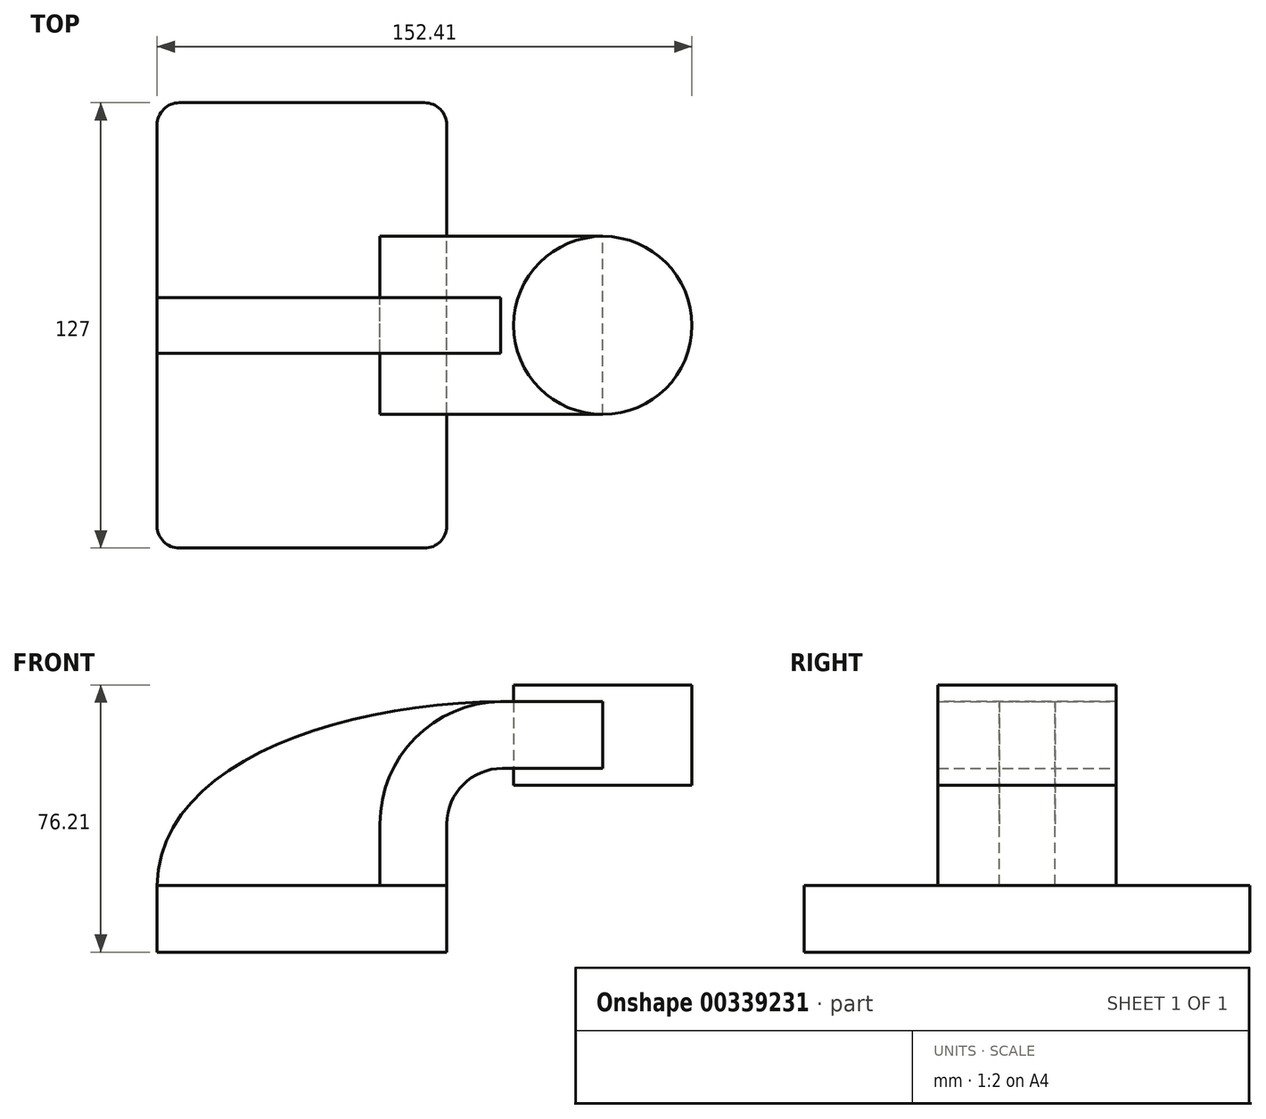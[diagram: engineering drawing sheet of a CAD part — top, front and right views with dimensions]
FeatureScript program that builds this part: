
annotation { "Feature Type Name" : "Feature", "Feature Type Description" : "" }
export const myFeature = defineFeature(function(context is Context, id is Id, definition is map)
    precondition{}
    {
        {
            var Q0;
            Q0=qCreatedBy(makeId("Front.planeOp"),FACE);
            var sketch = newSketch(context, id + "F0", { "sketchPlane" : qUnion([Q0])});
            skLineSegment(sketch, "E0.bottom", {"start": v(-41.28, -9.53) * mm, "end": v(41.28, -9.53) * mm});
            skLineSegment(sketch, "E0.top", {"start": v(-41.28, 9.52) * mm, "end": v(41.28, 9.52) * mm});
            skLineSegment(sketch, "E0.left", {"start": v(-41.28, -9.53) * mm, "end": v(-41.28, 9.53) * mm});
            skLineSegment(sketch, "E0.right", {"start": v(41.28, -9.53) * mm, "end": v(41.28, 9.52) * mm});
            skPoint(sketch, "E0.middle", {"position": v(0, 0) * mm});
            skLineSegment(sketch, "E1.bottom", {"start": v(60.32, 38.1) * mm, "end": v(111.12, 38.1) * mm});
            skLineSegment(sketch, "E1.top", {"start": v(60.32, 66.68) * mm, "end": v(111.12, 66.68) * mm});
            skLineSegment(sketch, "E1.left", {"start": v(60.32, 38.1) * mm, "end": v(60.32, 66.67) * mm});
            skLineSegment(sketch, "E1.right", {"start": v(111.12, 38.1) * mm, "end": v(111.12, 66.67) * mm});
            skPoint(sketch, "E1.middle", {"position": v(85.72, 52.39) * mm});
            skLineSegment(sketch, "E2", {"start": v(41.28, 9.52) * mm, "end": v(41.28, 27) * mm});
            skArc(sketch, "E3", {"start": v(41.28, 27) * mm, "mid": v(45.92, 38.23) * mm, "end": v(57.15, 42.88) * mm});
            skLineSegment(sketch, "E4", {"start": v(57.15, 42.88) * mm, "end": v(85.72, 42.88) * mm});
            skLineSegment(sketch, "E5.0", {"start": v(57.15, 61.93) * mm, "end": v(85.72, 61.93) * mm});
            skArc(sketch, "E5.1", {"start": v(22.23, 27) * mm, "mid": v(32.45, 51.7) * mm, "end": v(57.15, 61.93) * mm});
            skLineSegment(sketch, "E5.2", {"start": v(22.23, 9.52) * mm, "end": v(22.23, 27) * mm});
            skLineSegment(sketch, "E6", {"start": v(85.72, 38.1) * mm, "end": v(85.72, 66.68) * mm});
            skFitSpline(sketch, "E7", {"points": [v(-41.28, 9.53) * mm, v(57.15, 61.93) * mm], "startDerivative": vector(1.1, 104.22) * mm, "endDerivative": vector(139.4, 0.78) * mm});
            skSolve(sketch);
        }
        {
            var Q0;
            Q0=makeQuery(id+"F0.imprint","IMPRINT",FACE,{"disambiguationData":[TD([[makeQuery(id+"F0.imprint","IMPRINT",EDGE,{"derivedFrom":sQuery(id+"F0.wireOp",EDGE,"E0.bottom")}),1.0]])]});
            extrude(context, id + "F1", {"entities" : qUnion([Q0]), "endBound" : BoundingType.SYMMETRIC, "depth" : 127 * mm});
        }
        {
            var Q0;
            {var subQ1=sQuery(id+"F0.wireOp",EDGE,"E2");Q0=makeQuery(id+"F0.imprint","IMPRINT",FACE,{"disambiguationData":[TD([[makeQuery(id+"F0.imprint","IMPRINT",EDGE,{"derivedFrom":subQ1}),1.0]])]});}
            var Q1;
            {var subQ0=sQuery(id+"F0.wireOp",EDGE,"E4");var subQ1=sQuery(id+"F0.wireOp",EDGE,"E1.left");var subQ2=makeQuery(id+"F0.imprint","INTERSECT",VERTEX,{"derivedFrom":[subQ1,subQ0]});Q1=makeQuery(id+"F0.imprint","IMPRINT",FACE,{"disambiguationData":[TD([[makeQuery(id+"F0.imprint","IMPRINT",EDGE,{"disambiguationData":[TD([[subQ2,-1.0]])],"derivedFrom":subQ1}),-1.0]])]});}
            extrude(context, id + "F2", {"entities" : qUnion([Q0, Q1]), "endBound" : BoundingType.SYMMETRIC, "depth" : 50.8 * mm});
        }
        {
            var Q0;
            {var subQ3=sQuery(id+"F0.wireOp",EDGE,"E5.2");Q0=makeQuery(id+"F0.imprint","IMPRINT",FACE,{"disambiguationData":[TD([[makeQuery(id+"F0.imprint","IMPRINT",EDGE,{"derivedFrom":subQ3}),1.0]])]});}
            extrude(context, id + "F3", {"entities" : qUnion([Q0]), "endBound" : BoundingType.SYMMETRIC, "depth" : 15.88 * mm});
        }
        {
            var Q0;
            {var subQ4=sQuery(id+"F0.wireOp",EDGE,"E1.right");Q0=makeQuery(id+"F0.imprint","IMPRINT",FACE,{"disambiguationData":[TD([[makeQuery(id+"F0.imprint","IMPRINT",EDGE,{"derivedFrom":subQ4}),1.0]])]});}
            var Q1;
            Q1=sQuery(id+"F0.wireOp",EDGE,"E6");
            revolve(context, id + "F4", {"entities" : qUnion([Q0]), "axis" : qUnion([Q1]), "revolveType" : RevolveType.FULL});
        }
        {
            var Q0;
            Q0=makeQuery(id+"F1.opExtrude","CAP_EDGE",EDGE,{"disambiguationData":[OSD([sQuery(id+"F0.wireOp",EDGE,"E0.right")])],"isStart":false});
            var Q1;
            Q1=makeQuery(id+"F1.opExtrude","CAP_EDGE",EDGE,{"disambiguationData":[OSD([sQuery(id+"F0.wireOp",EDGE,"E0.right")])],"isStart":true});
            var Q2;
            Q2=makeQuery(id+"F1.opExtrude","CAP_EDGE",EDGE,{"disambiguationData":[OSD([sQuery(id+"F0.wireOp",EDGE,"E0.left")])],"isStart":true});
            var Q3;
            Q3=makeQuery(id+"F1.opExtrude","CAP_EDGE",EDGE,{"disambiguationData":[OSD([sQuery(id+"F0.wireOp",EDGE,"E0.left")])],"isStart":false});
            fillet(context, id + "F5", {"entities" : qUnion([Q0, Q1, Q2, Q3]), "radius" : 6.35 * mm, "tangentPropagation" : true, "allowEdgeOverflow" : false});
        }
    });
